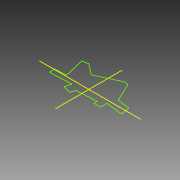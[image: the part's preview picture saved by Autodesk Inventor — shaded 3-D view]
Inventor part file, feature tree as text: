
AUTODESK INVENTOR PART (.ipt)
format: ipt  version: 2015 (Build 190159000, 159)  size: 64,512 bytes
history: native  units: mm
features: sketch x1
ambient origin geometry x8: Origin, YZ Plane, XZ Plane, XY Plane, X Axis, Y Axis, Z Axis, Center Point
feature tree (1):
  sketch  "Sketch1"
